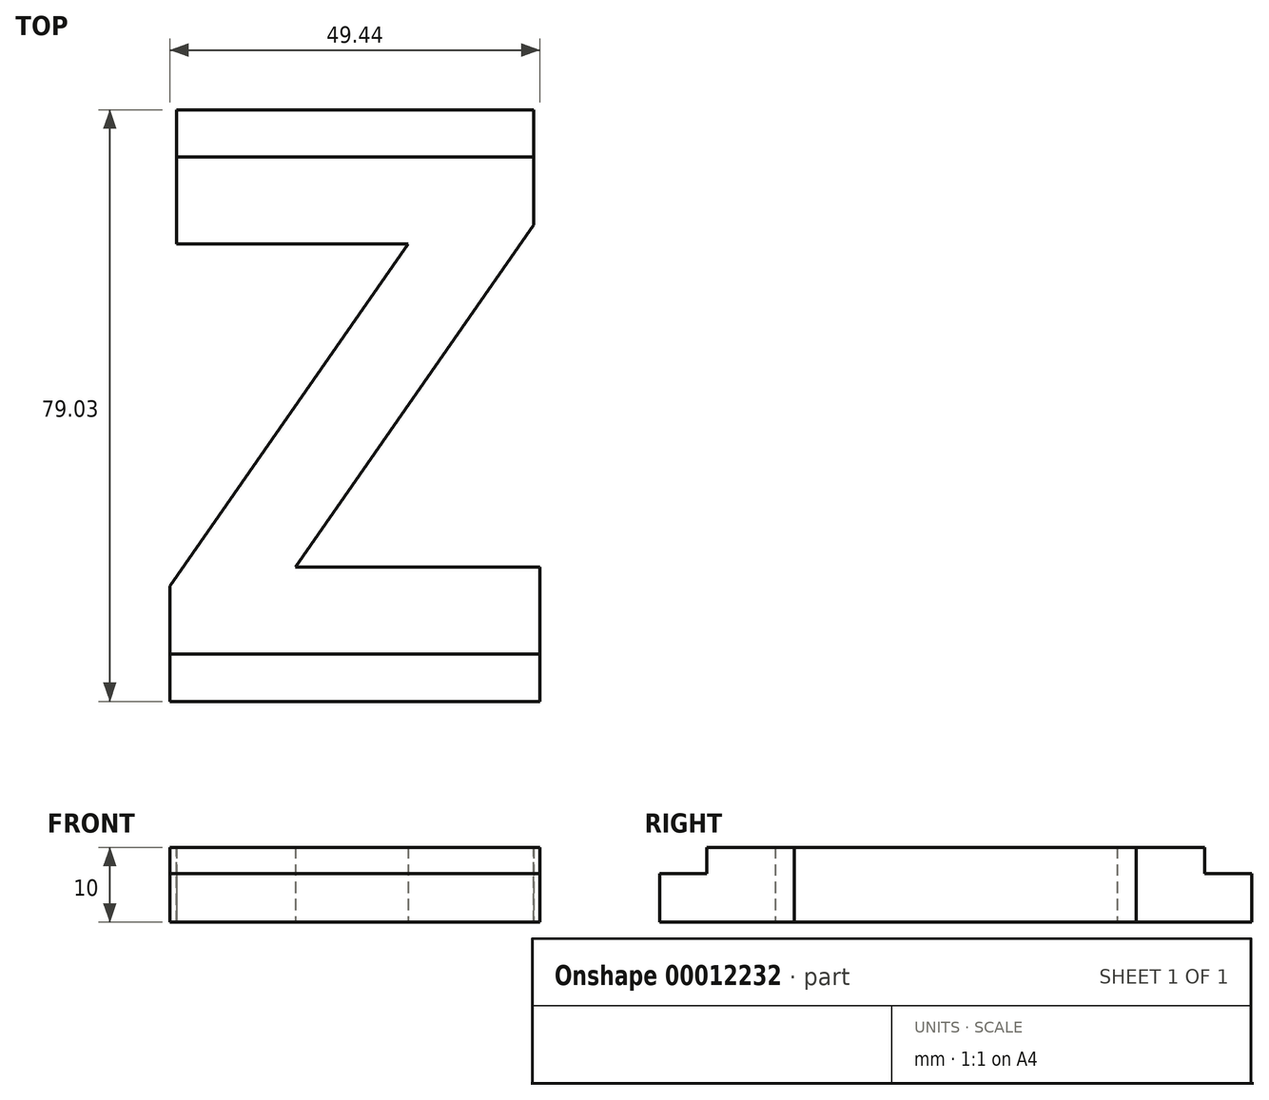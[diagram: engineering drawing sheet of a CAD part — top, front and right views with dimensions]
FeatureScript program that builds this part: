
annotation { "Feature Type Name" : "Feature", "Feature Type Description" : "" }
export const myFeature = defineFeature(function(context is Context, id is Id, definition is map)
    precondition{}
    {
        {
            var Q0;
            Q0=qCreatedBy(makeId("Top.planeOp"),FACE);
            var sketch = newSketch(context, id + "F0", { "sketchPlane" : qUnion([Q0])});
            skText(sketch, "E0", { "text": "Z\n", "fontName": "OpenSans-Bold.ttf"});
            const initialGuessF0  = {"E0": [-0.0577, 0, 1, 0, 0.067]};
            skSetInitialGuess(sketch, initialGuessF0);
            skSolve(sketch);
        }
        {
            var Q0;
            Q0=makeQuery(id+"F0.imprint","IMPRINT",FACE,{"disambiguationData":[TD([[makeQuery(id+"F0.imprint","IMPRINT",EDGE,{"derivedFrom":sQuery(id+"F0.wireOp",EDGE,"E0.sketch_text.stroke-0")}),-1.0]])]});
            extrude(context, id + "F1", {"entities" : qUnion([Q0]), "depth" : 10 * mm});
        }
        {
            var Q0;
            Q0=makeQuery(id+"F1.opExtrude","SWEPT_FACE",FACE,{"disambiguationData":[OSD([sQuery(id+"F0.wireOp",EDGE,"E0.sketch_text.stroke-0")])]});
            var sketch = newSketch(context, id + "F2", { "sketchPlane" : qUnion([Q0])});
            skLineSegment(sketch, "E1.bottom", {"start": v(-55.47, 0) * mm, "end": v(-6.03, 0) * mm});
            skLineSegment(sketch, "E1.top", {"start": v(-55.47, 6.5) * mm, "end": v(-6.03, 6.5) * mm});
            skLineSegment(sketch, "E1.left", {"start": v(-55.47, 0) * mm, "end": v(-55.47, 6.5) * mm});
            skLineSegment(sketch, "E1.right", {"start": v(-6.03, 0) * mm, "end": v(-6.03, 6.5) * mm});
            skSolve(sketch);
        }
        {
            var Q0;
            Q0=makeQuery(id+"F2.imprint","IMPRINT",FACE,{"disambiguationData":[TD([[makeQuery(id+"F2.imprint","IMPRINT",EDGE,{"derivedFrom":sQuery(id+"F2.wireOp",EDGE,"E1.bottom")}),-1.0]])]});
            extrude(context, id + "F3", {"entities" : qUnion([Q0]), "operationType" : NewBodyOperationType.ADD, "depth" : 6.3 * mm});
        }
        {
            var Q0;
            Q0=makeQuery(id+"F1.opExtrude","SWEPT_FACE",FACE,{"disambiguationData":[OSD([sQuery(id+"F0.wireOp",EDGE,"E0.sketch_text.stroke-5")])]});
            var sketch = newSketch(context, id + "F4", { "sketchPlane" : qUnion([Q0])});
            skLineSegment(sketch, "E2.bottom", {"start": v(6.9, 0) * mm, "end": v(54.6, 0) * mm});
            skLineSegment(sketch, "E2.top", {"start": v(6.9, 6.5) * mm, "end": v(54.6, 6.5) * mm});
            skLineSegment(sketch, "E2.left", {"start": v(6.9, 0) * mm, "end": v(6.9, 6.5) * mm});
            skLineSegment(sketch, "E2.right", {"start": v(54.6, 0) * mm, "end": v(54.6, 6.5) * mm});
            skSolve(sketch);
        }
        {
            var Q0;
            Q0 = qSketchRegion(id + "F4", true);
            extrude(context, id + "F5", {"entities" : qUnion([Q0]), "operationType" : NewBodyOperationType.ADD, "depth" : 6.3 * mm});
        }
    });
